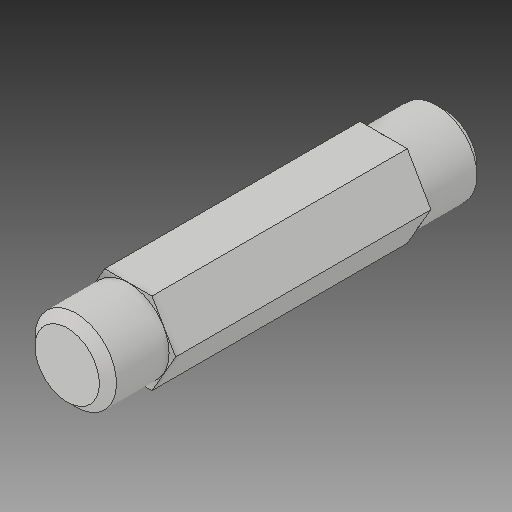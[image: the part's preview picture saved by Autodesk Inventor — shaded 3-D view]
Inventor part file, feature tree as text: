
AUTODESK INVENTOR PART (.ipt)
format: ipt  version: 2017 (Build 210142000, 142)  size: 92,672 bytes
history: native  units: in
note: dims shown in document units (in); Inventor stores cm internally (conversion verified against a paired STEP export)
features: chamfer x1
ambient origin geometry x8: Origin, YZ Plane, XZ Plane, XY Plane, X Axis, Y Axis, Z Axis, Center Point
bodies: Solid1 (feature_tree)
feature tree (1):
  chamfer  "Chamfer1"  [1 undecoded]
note: 1 required parameter value undecoded (feature->parameter linkage not recoverable at this tier; creation-order binding heuristic only, values carry confidence <= 0.55)
